FCSTD DOCUMENT  (FreeCAD 0.18R16117 (Git))
Label: printed_bearing
License: CreativeCommons Attribution-ShareAlike
LicenseURL: http://creativecommons.org/licenses/by-sa/4.0/
objects: Sketcher::SketchObject×1, PartDesign::Body×1
note: 2 computed .brp shape members not serialized (recipe doc carries the construction recipe); baked Part::Feature solids carry a one-line shape summary decoded from their .brp

FEATURE [Sketcher::SketchObject] Sketch
  MapMode = 5
  Support = -> [XY_Plane]
  sketch-geometry (15):
    g0: Circle CenterX=0 CenterY=0 CenterZ=0 NormalX=0 NormalY=0 NormalZ=1 AngleXU=0 Radius=4
    g1: Circle CenterX=0 CenterY=0 CenterZ=0 NormalX=0 NormalY=0 NormalZ=1 AngleXU=0 Radius=4.93485
    g2: Circle CenterX=0 CenterY=0 CenterZ=0 NormalX=0 NormalY=0 NormalZ=1 AngleXU=0 Radius=11
    g3: Circle CenterX=0 CenterY=0 CenterZ=0 NormalX=0 NormalY=0 NormalZ=1 AngleXU=0 Radius=10.0652
    g4: LineSegment [constr] StartX=4 StartY=0 StartZ=0 EndX=4.93485 EndY=0 EndZ=0
    g5: LineSegment [constr] StartX=10.0652 StartY=0 StartZ=0 EndX=11 EndY=0 EndZ=0
    g6: Circle CenterX=7.5 CenterY=0 CenterZ=0 NormalX=0 NormalY=0 NormalZ=1 AngleXU=0 Radius=2.56515
    g7: Circle CenterX=5.74533 CenterY=-4.82091 CenterZ=0 NormalX=0 NormalY=0 NormalZ=1 AngleXU=0 Radius=2.56515
    g8: Circle CenterX=1.30236 CenterY=-7.38606 CenterZ=0 NormalX=0 NormalY=0 NormalZ=1 AngleXU=0 Radius=2.56515
    g9: Circle CenterX=-3.75 CenterY=-6.49519 CenterZ=0 NormalX=0 NormalY=0 NormalZ=1 AngleXU=0 Radius=2.56515
    g10: Circle CenterX=-7.04769 CenterY=-2.56515 CenterZ=0 NormalX=0 NormalY=0 NormalZ=1 AngleXU=0 Radius=2.56515
    g11: Circle CenterX=-7.04769 CenterY=2.56515 CenterZ=0 NormalX=0 NormalY=0 NormalZ=1 AngleXU=0 Radius=2.56515
    g12: Circle CenterX=-3.75 CenterY=6.49519 CenterZ=0 NormalX=0 NormalY=0 NormalZ=1 AngleXU=0 Radius=2.56515
    g13: Circle CenterX=1.30236 CenterY=7.38606 CenterZ=0 NormalX=0 NormalY=0 NormalZ=1 AngleXU=0 Radius=2.56515
    g14: Circle CenterX=5.74533 CenterY=4.82091 CenterZ=0 NormalX=0 NormalY=0 NormalZ=1 AngleXU=0 Radius=2.56515
  constraints (46):
    c: Coincident(g0,g-1)
    c: Coincident(g1,g0)
    c: Coincident(g2,g0)
    c: Coincident(g3,g0)
    c: Radius(g0) = 4
    c: Radius(g2) = 11
    c: PointOnObject(g4,g0)
    c: PointOnObject(g4,g1)
    c: Horizontal(g4)
    c: PointOnObject(g5,g3)
    c: PointOnObject(g5,g2)
    c: Horizontal(g5)
    c: Equal(g4,g5)
    c: PointOnObject(g0,g4)
    c: PointOnObject(g0,g5)
    c: Equal(g13,g14)
    c: Equal(g14,g6)
    c: Equal(g6,g12)
    c: Equal(g12,g11)
    c: Equal(g11,g7)
    c: Equal(g7,g8)
    c: Equal(g8,g9)
    c: Equal(g9,g10)
    c: Tangent(g6,g3)
    c: Tangent(g14,g3)
    c: Tangent(g13,g3)
    c: Tangent(g12,g3)
    c: Tangent(g11,g3)
    c: Tangent(g10,g3)
    c: Tangent(g9,g3)
    c: Tangent(g8,g3)
    c: Tangent(g7,g3)
    c: Tangent(g7,g1)
    c: Tangent(g9,g8)
    c: Tangent(g9,g10)
    c: Tangent(g11,g10)
    c: Tangent(g12,g11)
    c: Tangent(g8,g7)
    c: Tangent(g7,g6)
    c: Tangent(g6,g14)
    c: Tangent(g13,g12)
    c: Tangent(g13,g14)
    c: PointOnObject(g6,g5)
    c: Radius(g6) = 2.56515
    c: Distance(g5) = 0.934849
    c: Distance(g6,g0) = 7.5
FEATURE [PartDesign::Body] Body
  Group = -> [Sketch]
  Origin = -> Origin
